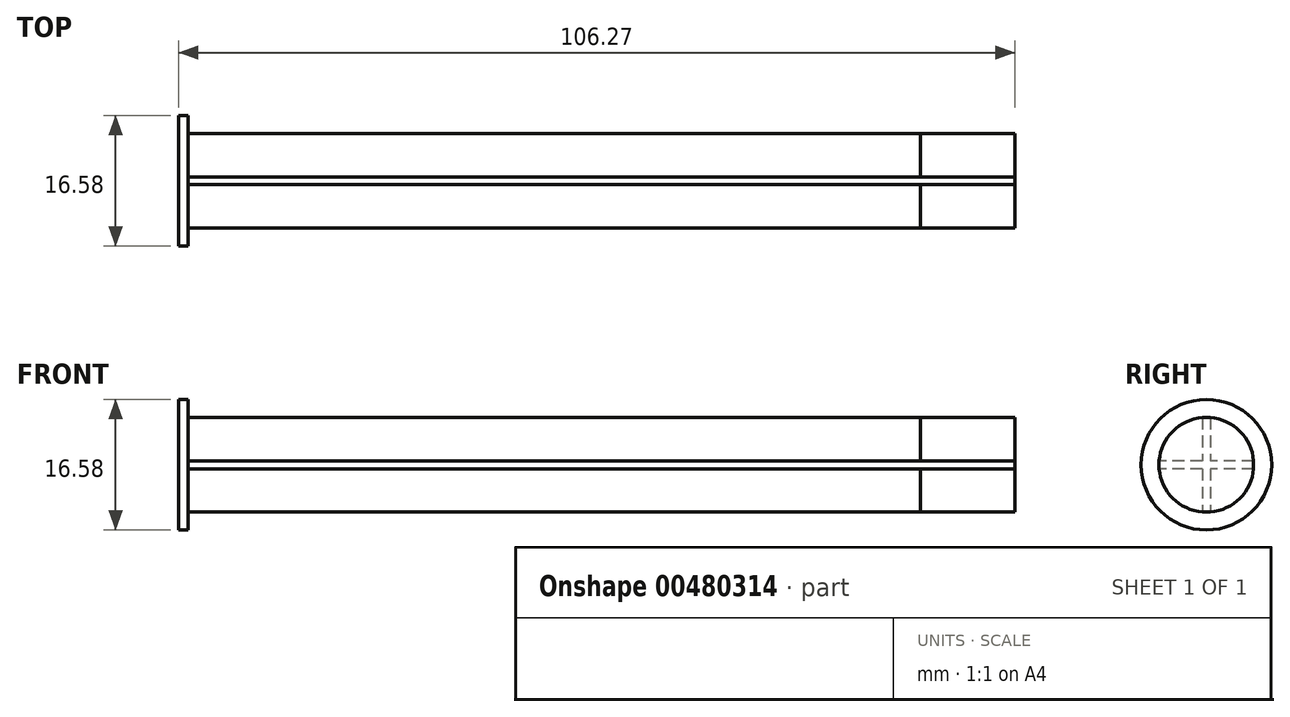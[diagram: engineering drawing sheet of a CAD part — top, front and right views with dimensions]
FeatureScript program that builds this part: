
annotation { "Feature Type Name" : "Feature", "Feature Type Description" : "" }
export const myFeature = defineFeature(function(context is Context, id is Id, definition is map)
    precondition{}
    {
        {
            var Q0;
            Q0=qCreatedBy(makeId("Right.planeOp"),FACE);
            var sketch = newSketch(context, id + "F0", { "sketchPlane" : qUnion([Q0])});
            skLineSegment(sketch, "E0.bottom", {"start": v(-0.5, 6) * mm, "end": v(0.5, 6) * mm});
            skLineSegment(sketch, "E0.top", {"start": v(-0.5, -6) * mm, "end": v(0.5, -6) * mm});
            skLineSegment(sketch, "E0.left", {"start": v(-0.5, 6) * mm, "end": v(-0.5, -6) * mm});
            skLineSegment(sketch, "E0.right", {"start": v(0.5, 6) * mm, "end": v(0.5, -6) * mm});
            skPoint(sketch, "E0.middle", {"position": v(0, 0) * mm});
            skLineSegment(sketch, "E1.bottom", {"start": v(6, -0.5) * mm, "end": v(-6, -0.5) * mm});
            skLineSegment(sketch, "E1.top", {"start": v(6, 0.5) * mm, "end": v(-6, 0.5) * mm});
            skLineSegment(sketch, "E1.left", {"start": v(6, -0.5) * mm, "end": v(6, 0.5) * mm});
            skLineSegment(sketch, "E1.right", {"start": v(-6, -0.5) * mm, "end": v(-6, 0.5) * mm});
            skSolve(sketch);
        }
        {
            var Q0;
            {var subQ0=sQuery(id+"F0.wireOp",EDGE,"E0.bottom");Q0=makeQuery(id+"F0.imprint","IMPRINT",FACE,{"disambiguationData":[TD([[makeQuery(id+"F0.imprint","IMPRINT",EDGE,{"derivedFrom":subQ0}),-1.0]])]});}
            var Q1;
            {var subQ0=sQuery(id+"F0.wireOp",EDGE,"E1.top");var subQ1=sQuery(id+"F0.wireOp",EDGE,"E0.left");var subQ2=makeQuery(id+"F0.imprint","INTERSECT",VERTEX,{"derivedFrom":[subQ1,subQ0]});Q1=makeQuery(id+"F0.imprint","IMPRINT",FACE,{"disambiguationData":[TD([[makeQuery(id+"F0.imprint","IMPRINT",EDGE,{"disambiguationData":[TD([[subQ2,-1.0]])],"derivedFrom":subQ1}),1.0]])]});}
            var Q2;
            {var subQ5=sQuery(id+"F0.wireOp",EDGE,"E1.left");Q2=makeQuery(id+"F0.imprint","IMPRINT",FACE,{"disambiguationData":[TD([[makeQuery(id+"F0.imprint","IMPRINT",EDGE,{"derivedFrom":subQ5}),1.0]])]});}
            var Q3;
            {var subQ5=sQuery(id+"F0.wireOp",EDGE,"E1.right");Q3=makeQuery(id+"F0.imprint","IMPRINT",FACE,{"disambiguationData":[TD([[makeQuery(id+"F0.imprint","IMPRINT",EDGE,{"derivedFrom":subQ5}),-1.0]])]});}
            var Q4;
            {var subQ0=sQuery(id+"F0.wireOp",EDGE,"E0.top");Q4=makeQuery(id+"F0.imprint","IMPRINT",FACE,{"disambiguationData":[TD([[makeQuery(id+"F0.imprint","IMPRINT",EDGE,{"derivedFrom":subQ0}),1.0]])]});}
            extrude(context, id + "F1", {"entities" : qUnion([Q0, Q1, Q2, Q3, Q4]), "depth" : 93.07 * mm});
        }
        {
            var Q0;
            Q0=makeQuery(id+"F1.opExtrude","CAP_FACE",FACE,{"disambiguationData":[OSD([sQuery(id+"F0.wireOp",EDGE,"E0.bottom"),sQuery(id+"F0.wireOp",EDGE,"E0.top"),sQuery(id+"F0.wireOp",EDGE,"E0.left"),sQuery(id+"F0.wireOp",EDGE,"E0.right"),sQuery(id+"F0.wireOp",EDGE,"E1.bottom"),sQuery(id+"F0.wireOp",EDGE,"E1.top"),sQuery(id+"F0.wireOp",EDGE,"E1.left"),sQuery(id+"F0.wireOp",EDGE,"E1.right")])],"isStart":false});
            var sketch = newSketch(context, id + "F2", { "sketchPlane" : qUnion([Q0])});
            skCircle(sketch, "E2", {"center": v(0, 0) * mm, "radius": 6.02 * mm});
            skSolve(sketch);
        }
        {
            var Q0;
            {var subQ1=sQuery(id+"F0.wireOp",EDGE,"E0.left");var subQ2=sQuery(id+"F0.wireOp",EDGE,"E0.top");var subQ5=makeQuery(id+"F1.opExtrude","CAP_EDGE",EDGE,{"disambiguationData":[OSD([subQ1]),TDD([makeQuery(id+"F0.imprint","IMPRINT",EDGE,{"disambiguationData":[TD([[makeQuery(id+"F0.imprint","INTERSECT",VERTEX,{"derivedFrom":[subQ2,subQ1]}),1.0]])],"derivedFrom":subQ1})])],"isStart":false});Q0=makeQuery(id+"F2.imprint","IMPRINT",FACE,{"disambiguationData":[TD([[makeQuery(id+"F2.imprint","IMPRINT",EDGE,{"derivedFrom":subQ5}),-1.0]])]});}
            var Q1;
            {var subQ1=sQuery(id+"F0.wireOp",EDGE,"E0.right");var subQ2=sQuery(id+"F0.wireOp",EDGE,"E0.top");var subQ5=makeQuery(id+"F1.opExtrude","CAP_EDGE",EDGE,{"disambiguationData":[OSD([subQ1]),TDD([makeQuery(id+"F0.imprint","IMPRINT",EDGE,{"disambiguationData":[TD([[makeQuery(id+"F0.imprint","INTERSECT",VERTEX,{"derivedFrom":[subQ2,subQ1]}),1.0]])],"derivedFrom":subQ1})])],"isStart":false});Q1=makeQuery(id+"F2.imprint","IMPRINT",FACE,{"disambiguationData":[TD([[makeQuery(id+"F2.imprint","IMPRINT",EDGE,{"derivedFrom":subQ5}),1.0]])]});}
            var Q2;
            {var subQ11=sQuery(id+"F0.wireOp",EDGE,"E0.bottom");Q2=makeQuery(id+"F2.imprint","IMPRINT",FACE,{"disambiguationData":[TD([[makeQuery(id+"F2.imprint","IMPRINT",EDGE,{"derivedFrom":makeQuery(id+"F1.opExtrude","CAP_EDGE",EDGE,{"disambiguationData":[OSD([subQ11])],"isStart":false})}),-1.0]])]});}
            var Q3;
            {var subQ1=sQuery(id+"F0.wireOp",EDGE,"E0.left");var subQ2=sQuery(id+"F0.wireOp",EDGE,"E0.bottom");var subQ5=makeQuery(id+"F1.opExtrude","CAP_EDGE",EDGE,{"disambiguationData":[OSD([subQ1]),TDD([makeQuery(id+"F0.imprint","IMPRINT",EDGE,{"disambiguationData":[TD([[makeQuery(id+"F0.imprint","INTERSECT",VERTEX,{"derivedFrom":[subQ2,subQ1]}),-1.0]])],"derivedFrom":subQ1})])],"isStart":false});Q3=makeQuery(id+"F2.imprint","IMPRINT",FACE,{"disambiguationData":[TD([[makeQuery(id+"F2.imprint","IMPRINT",EDGE,{"derivedFrom":subQ5}),-1.0]])]});}
            var Q4;
            {var subQ1=sQuery(id+"F0.wireOp",EDGE,"E0.right");var subQ2=sQuery(id+"F0.wireOp",EDGE,"E0.bottom");var subQ5=makeQuery(id+"F1.opExtrude","CAP_EDGE",EDGE,{"disambiguationData":[OSD([subQ1]),TDD([makeQuery(id+"F0.imprint","IMPRINT",EDGE,{"disambiguationData":[TD([[makeQuery(id+"F0.imprint","INTERSECT",VERTEX,{"derivedFrom":[subQ2,subQ1]}),-1.0]])],"derivedFrom":subQ1})])],"isStart":false});Q4=makeQuery(id+"F2.imprint","IMPRINT",FACE,{"disambiguationData":[TD([[makeQuery(id+"F2.imprint","IMPRINT",EDGE,{"derivedFrom":subQ5}),1.0]])]});}
            extrude(context, id + "F3", {"entities" : qUnion([Q0, Q1, Q2, Q3, Q4]), "operationType" : NewBodyOperationType.ADD, "depth" : 12 * mm});
        }
        {
            var Q0;
            Q0=makeQuery(id+"F1.opExtrude","CAP_FACE",FACE,{"disambiguationData":[OSD([sQuery(id+"F0.wireOp",EDGE,"E0.bottom"),sQuery(id+"F0.wireOp",EDGE,"E0.top"),sQuery(id+"F0.wireOp",EDGE,"E0.left"),sQuery(id+"F0.wireOp",EDGE,"E0.right"),sQuery(id+"F0.wireOp",EDGE,"E1.bottom"),sQuery(id+"F0.wireOp",EDGE,"E1.top"),sQuery(id+"F0.wireOp",EDGE,"E1.left"),sQuery(id+"F0.wireOp",EDGE,"E1.right")])],"isStart":true});
            var sketch = newSketch(context, id + "F4", { "sketchPlane" : qUnion([Q0])});
            skCircle(sketch, "E3", {"center": v(0, 0) * mm, "radius": 8.29 * mm});
            skSolve(sketch);
        }
        {
            var Q0;
            {var subQ0=sQuery(id+"F0.wireOp",EDGE,"E1.left");Q0=makeQuery(id+"F4.imprint","IMPRINT",FACE,{"disambiguationData":[TD([[makeQuery(id+"F4.imprint","IMPRINT",EDGE,{"derivedFrom":makeQuery(id+"F1.opExtrude","CAP_EDGE",EDGE,{"disambiguationData":[OSD([subQ0])],"isStart":true})}),1.0]])]});}
            var Q1;
            {var subQ5=sQuery(id+"F0.wireOp",EDGE,"E1.right");Q1=makeQuery(id+"F4.imprint","IMPRINT",FACE,{"disambiguationData":[TD([[makeQuery(id+"F4.imprint","IMPRINT",EDGE,{"derivedFrom":makeQuery(id+"F1.opExtrude","CAP_EDGE",EDGE,{"disambiguationData":[OSD([subQ5])],"isStart":true})}),-1.0]])]});}
            var Q2;
            {var subQ11=sQuery(id+"F0.wireOp",EDGE,"E0.bottom");Q2=makeQuery(id+"F4.imprint","IMPRINT",FACE,{"disambiguationData":[TD([[makeQuery(id+"F4.imprint","IMPRINT",EDGE,{"derivedFrom":makeQuery(id+"F1.opExtrude","CAP_EDGE",EDGE,{"disambiguationData":[OSD([subQ11])],"isStart":true})}),1.0]])]});}
            extrude(context, id + "F5", {"entities" : qUnion([Q0, Q1, Q2]), "operationType" : NewBodyOperationType.ADD, "depth" : 1 * mm});
        }
        {
            var Q0;
            Q0=makeQuery(id+"F4.imprint","IMPRINT",FACE,{"disambiguationData":[TD([[makeQuery(id+"F4.imprint","IMPRINT",EDGE,{"derivedFrom":sQuery(id+"F4.wireOp",EDGE,"E3")}),1.0]])]});
            extrude(context, id + "F6", {"entities" : qUnion([Q0]), "operationType" : NewBodyOperationType.ADD, "depth" : 1.2 * mm});
        }
        {
            var Q0;
            {var subQ11=sQuery(id+"F0.wireOp",EDGE,"E0.bottom");Q0=makeQuery(id+"F4.imprint","IMPRINT",FACE,{"disambiguationData":[TD([[makeQuery(id+"F4.imprint","IMPRINT",EDGE,{"derivedFrom":makeQuery(id+"F1.opExtrude","CAP_EDGE",EDGE,{"disambiguationData":[OSD([subQ11])],"isStart":true})}),1.0]])]});}
            extrude(context, id + "F7", {"entities" : qUnion([Q0]), "operationType" : NewBodyOperationType.ADD, "depth" : 1.2 * mm});
        }
    });
